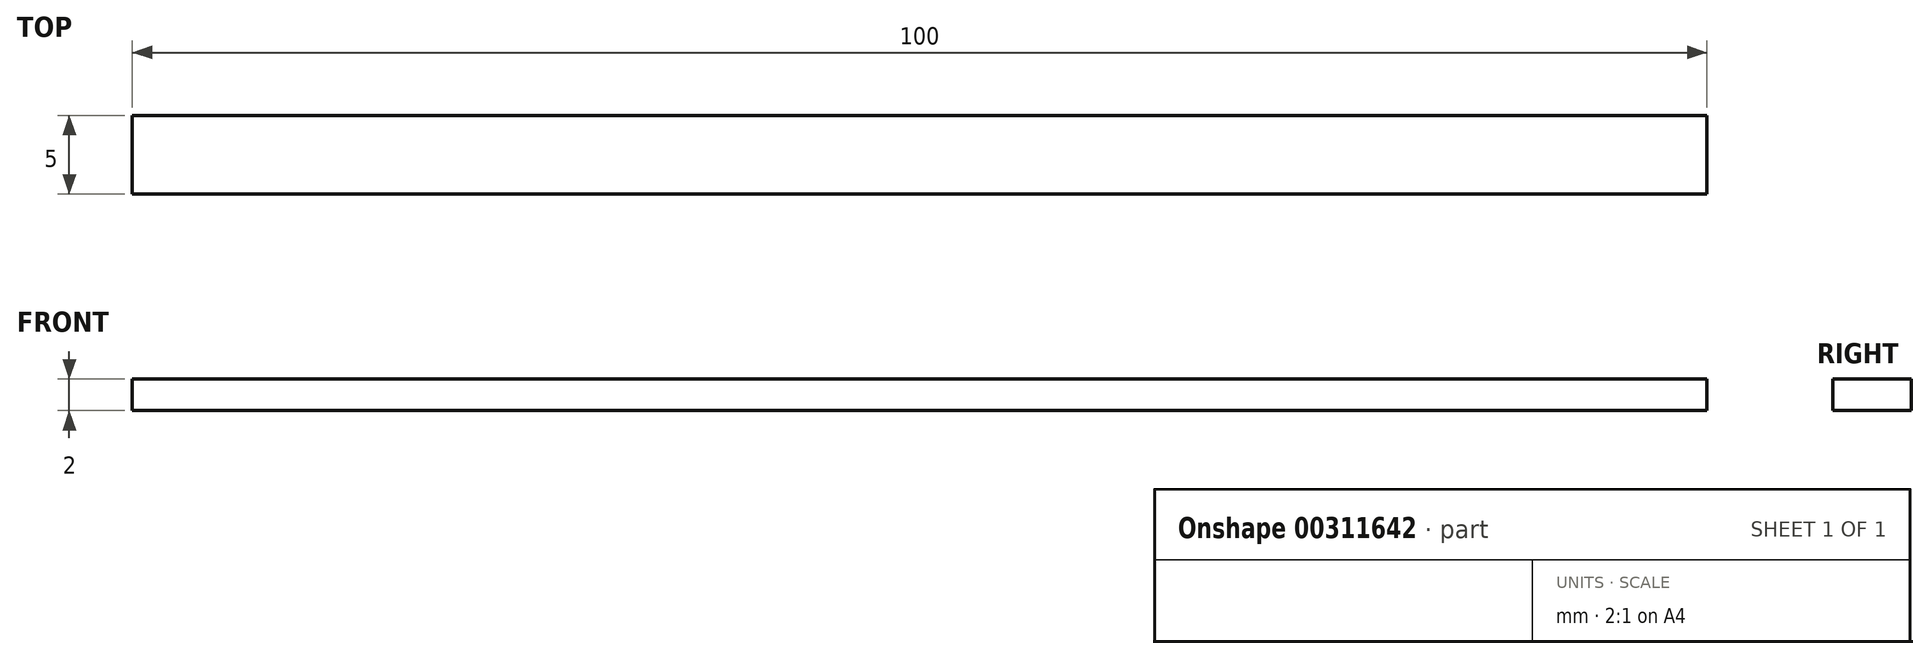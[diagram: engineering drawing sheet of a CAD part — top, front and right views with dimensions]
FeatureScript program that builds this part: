
annotation { "Feature Type Name" : "Feature", "Feature Type Description" : "" }
export const myFeature = defineFeature(function(context is Context, id is Id, definition is map)
    precondition{}
    {
        {
            var Q0;
            Q0=qCreatedBy(makeId("Right.planeOp"),FACE);
            var sketch = newSketch(context, id + "F0", { "sketchPlane" : qUnion([Q0])});
            skLineSegment(sketch, "E0.bottom", {"start": v(0, 0) * mm, "end": v(5, 0) * mm});
            skLineSegment(sketch, "E0.top", {"start": v(0, 2) * mm, "end": v(5, 2) * mm});
            skLineSegment(sketch, "E0.left", {"start": v(0, 0) * mm, "end": v(0, 2) * mm});
            skLineSegment(sketch, "E0.right", {"start": v(5, 0) * mm, "end": v(5, 2) * mm});
            skSolve(sketch);
        }
        {
            var Q0;
            Q0=makeQuery(id+"F0.imprint","IMPRINT",FACE,{"disambiguationData":[TD([[makeQuery(id+"F0.imprint","IMPRINT",EDGE,{"derivedFrom":sQuery(id+"F0.wireOp",EDGE,"E0.bottom")}),1.0]])]});
            extrude(context, id + "F1", {"entities" : qUnion([Q0]), "depth" : 70 * mm});
        }
        {
            var Q0;
            Q0=makeQuery(id+"F1.opExtrude","CAP_FACE",FACE,{"disambiguationData":[OSD([sQuery(id+"F0.wireOp",EDGE,"E0.bottom"),sQuery(id+"F0.wireOp",EDGE,"E0.top"),sQuery(id+"F0.wireOp",EDGE,"E0.left"),sQuery(id+"F0.wireOp",EDGE,"E0.right")])],"isStart":false});
            extrude(context, id + "F2", {"entities" : qUnion([Q0]), "operationType" : NewBodyOperationType.ADD, "depth" : 30 * mm});
        }
    });
